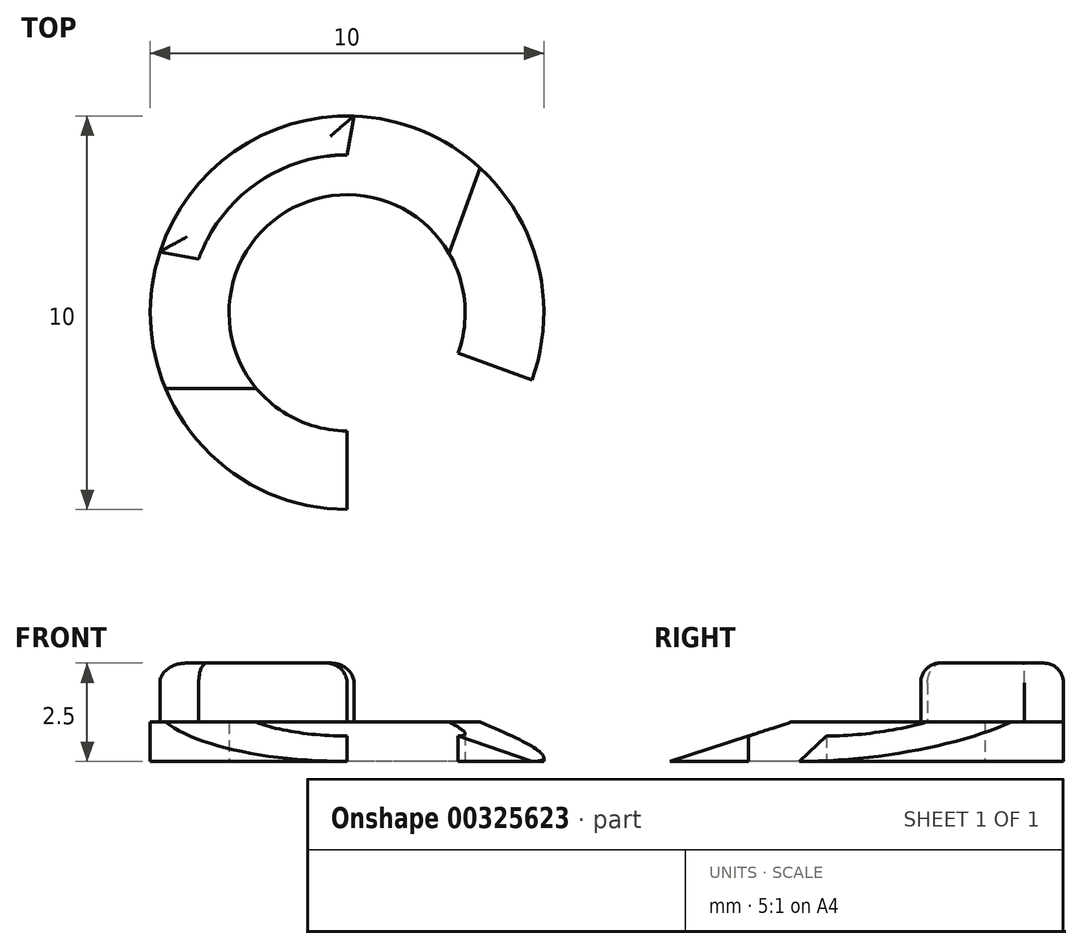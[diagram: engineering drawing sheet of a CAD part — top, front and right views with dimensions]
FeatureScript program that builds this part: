
annotation { "Feature Type Name" : "Feature", "Feature Type Description" : "" }
export const myFeature = defineFeature(function(context is Context, id is Id, definition is map)
    precondition{}
    {
        {
            var Q0;
            Q0=qCreatedBy(makeId("Top.planeOp"),FACE);
            var sketch = newSketch(context, id + "F0", { "sketchPlane" : qUnion([Q0])});
            skArc(sketch, "E0", {"start": v(2.82, -1.03) * mm, "mid": v(-1.72, 2.46) * mm, "end": v(0, -3) * mm});
            skArc(sketch, "E1.0", {"start": v(4.7, -1.71) * mm, "mid": v(-2.87, 4.1) * mm, "end": v(0, -5) * mm});
            skLineSegment(sketch, "E2", {"start": v(0, -3) * mm, "end": v(0, -5) * mm});
            skLineSegment(sketch, "E3", {"start": v(2.82, -1.03) * mm, "end": v(4.7, -1.71) * mm});
            skLineSegment(sketch, "E4", {"start": v(0, 0) * mm, "end": v(-8.02, 11.45) * mm, "construction": true});
            skLineSegment(sketch, "E5", {"start": v(-3.94, 0.7) * mm, "end": v(-4.92, 0.87) * mm});
            skLineSegment(sketch, "E6", {"start": v(0.7, 3.94) * mm, "end": v(0.87, 4.92) * mm});
            skArc(sketch, "E7", {"start": v(0.7, 3.94) * mm, "mid": v(-2.3, 3.28) * mm, "end": v(-3.94, 0.7) * mm});
            skSolve(sketch);
        }
        {
            var Q0;
            Q0 = qSketchRegion(id + "F0", true);
            extrude(context, id + "F1", {"entities" : qUnion([Q0]), "depth" : 1 * mm});
        }
        {
            var Q0;
            Q0=makeQuery(id+"F1.opExtrude","SWEPT_FACE",FACE,{"disambiguationData":[OSD([sQuery(id+"F0.wireOp",EDGE,"E3")])]});
            var sketch = newSketch(context, id + "F2", { "sketchPlane" : qUnion([Q0])});
            skLineSegment(sketch, "E8", {"start": v(5, 0) * mm, "end": v(1.92, 1) * mm});
            skLineSegment(sketch, "E9", {"start": v(1.92, 1) * mm, "end": v(5, 1) * mm});
            skLineSegment(sketch, "E10", {"start": v(5, 1) * mm, "end": v(5, 0) * mm});
            skLineSegment(sketch, "E11.0", {"start": v(3, 1) * mm, "end": v(5, 1) * mm});
            skSolve(sketch);
        }
        {
            var Q0;
            {var subQ0=sQuery(id+"F2.wireOp",EDGE,"E10");Q0=makeQuery(id+"F2.imprint","IMPRINT",FACE,{"disambiguationData":[TD([[makeQuery(id+"F2.imprint","IMPRINT",EDGE,{"derivedFrom":subQ0}),-1.0]])]});}
            var Q1;
            {var subQ0=sQuery(id+"F2.wireOp",EDGE,"E9");Q1=makeQuery(id+"F2.imprint","IMPRINT",FACE,{"disambiguationData":[TD([[makeQuery(id+"F2.imprint","IMPRINT",EDGE,{"derivedFrom":subQ0}),-1.0]])]});}
            extrude(context, id + "F3", {"entities" : qUnion([Q0, Q1]), "operationType" : NewBodyOperationType.REMOVE, "oppositeDirection" : true, "depth" : 25 * mm});
        }
        {
            var Q0;
            Q0=makeQuery(id+"F1.opExtrude","SWEPT_FACE",FACE,{"disambiguationData":[OSD([sQuery(id+"F0.wireOp",EDGE,"E2")])]});
            var sketch = newSketch(context, id + "F4", { "sketchPlane" : qUnion([Q0])});
            skLineSegment(sketch, "E12", {"start": v(-5, 0) * mm, "end": v(-5, 1) * mm});
            skLineSegment(sketch, "E13", {"start": v(-5, 1) * mm, "end": v(-1.92, 1) * mm});
            skLineSegment(sketch, "E14", {"start": v(-1.92, 1) * mm, "end": v(-5, 0) * mm});
            skSolve(sketch);
        }
        {
            var Q0;
            Q0 = qSketchRegion(id + "F4", true);
            extrude(context, id + "F5", {"entities" : qUnion([Q0]), "operationType" : NewBodyOperationType.REMOVE, "oppositeDirection" : true, "depth" : 25 * mm});
        }
        {
            var Q0;
            Q0=makeQuery(id+"F1.opExtrude","CAP_FACE",FACE,{"disambiguationData":[OSD([sQuery(id+"F0.wireOp",EDGE,"E0"),sQuery(id+"F0.wireOp",EDGE,"E1.0"),sQuery(id+"F0.wireOp",EDGE,"E2"),sQuery(id+"F0.wireOp",EDGE,"E3")])],"isStart":false});
            var sketch = newSketch(context, id + "F6", { "sketchPlane" : qUnion([Q0])});
            skLineSegment(sketch, "E15", {"start": v(-5.97, 8.53) * mm, "end": v(5.92, -8.45) * mm, "construction": true});
            skArc(sketch, "E16", {"start": v(0, 4.01) * mm, "mid": v(-2.3, 3.29) * mm, "end": v(-3.77, 1.37) * mm});
            skLineSegment(sketch, "E17", {"start": v(-3.77, 1.37) * mm, "end": v(-1.89, 2.7) * mm, "construction": true});
            skLineSegment(sketch, "E18", {"start": v(-1.89, 2.7) * mm, "end": v(0, 4.01) * mm, "construction": true});
            skLineSegment(sketch, "E19", {"start": v(0, 4.01) * mm, "end": v(0.17, 5) * mm});
            skLineSegment(sketch, "E20", {"start": v(-3.77, 1.37) * mm, "end": v(-4.76, 1.55) * mm});
            skSolve(sketch);
        }
        {
            var Q0;
            Q0 = qSketchRegion(id + "F6", true);
            var Q1;
            Q1=makeQuery(id+"F6.imprint","IMPRINT",FACE,{"disambiguationData":[TD([[makeQuery(id+"F6.imprint","IMPRINT",EDGE,{"derivedFrom":sQuery(id+"F6.wireOp",EDGE,"E16")}),-1.0]])]});
            extrude(context, id + "F7", {"entities" : qUnion([Q0, Q1]), "operationType" : NewBodyOperationType.ADD, "depth" : 1.5 * mm});
        }
        {
            var Q0;
            Q0=makeQuery(id+"F7.opExtrude","CAP_EDGE",EDGE,{"disambiguationData":[OSD([sQuery(id+"F6.wireOp",EDGE,"E20")])],"isStart":false});
            var Q1;
            Q1=makeQuery(id+"F7.opExtrude","CAP_EDGE",EDGE,{"disambiguationData":[OSD([sQuery(id+"F6.wireOp",EDGE,"E19")])],"isStart":false});
            var Q2;
            Q2=makeQuery(id+"F7.opExtrude","CAP_EDGE",EDGE,{"disambiguationData":[OSD([sQuery(id+"F0.wireOp",EDGE,"E1.0")])],"isStart":false});
            fillet(context, id + "F8", {"entities" : qUnion([Q0, Q1, Q2]), "radius" : .5 * mm, "tangentPropagation" : true, "allowEdgeOverflow" : false});
        }
    });
